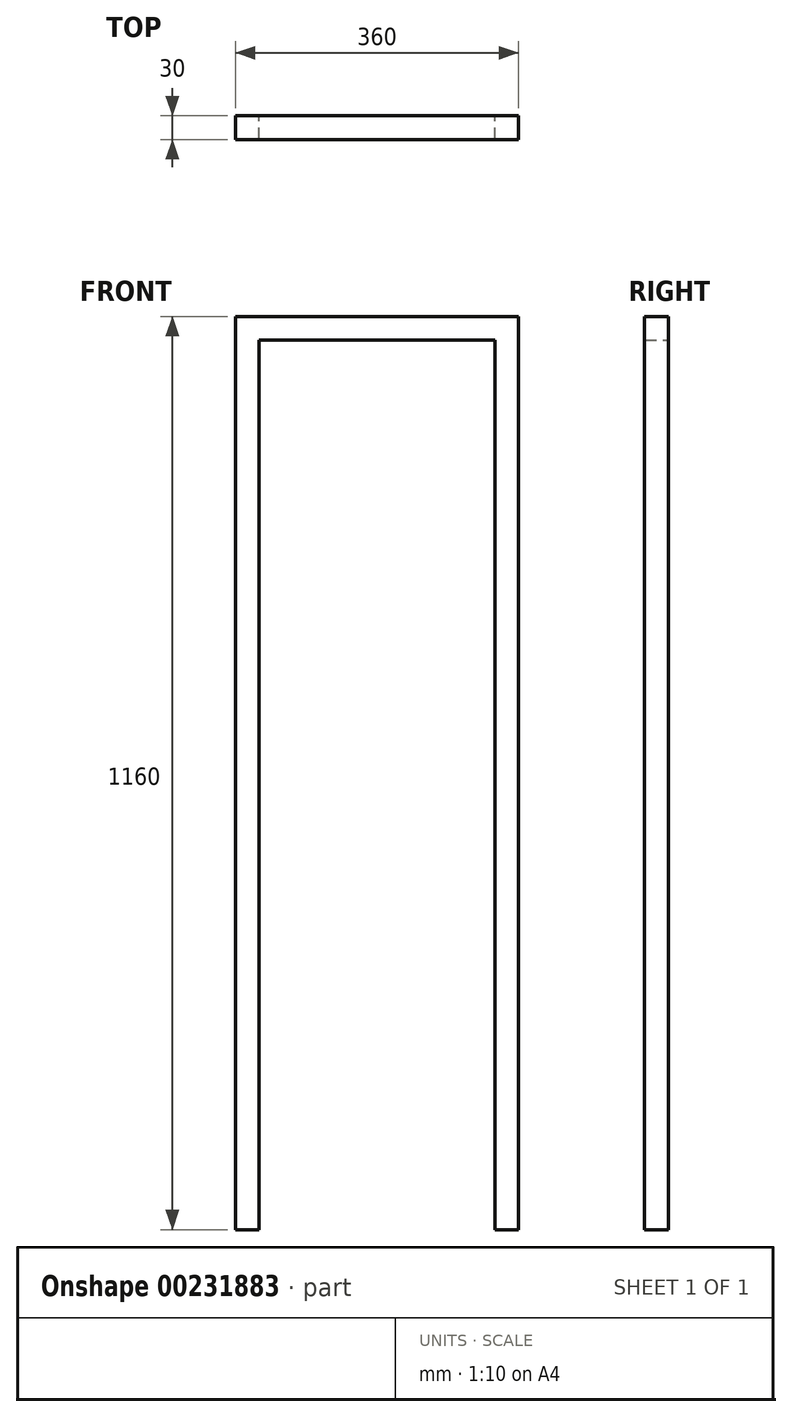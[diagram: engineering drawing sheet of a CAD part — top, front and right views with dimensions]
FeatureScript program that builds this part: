
annotation { "Feature Type Name" : "Feature", "Feature Type Description" : "" }
export const myFeature = defineFeature(function(context is Context, id is Id, definition is map)
    precondition{}
    {
        {
            var Q0;
            Q0=qCreatedBy(makeId("Front.planeOp"),FACE);
            var sketch = newSketch(context, id + "F0", { "sketchPlane" : qUnion([Q0])});
            skLineSegment(sketch, "E0.top", {"start": v(0, 1130) * mm, "end": v(-300, 1130) * mm});
            skLineSegment(sketch, "E0.left", {"start": v(0, 0) * mm, "end": v(0, 1130) * mm});
            skLineSegment(sketch, "E0.right", {"start": v(-300, 0) * mm, "end": v(-300, 1130) * mm});
            skLineSegment(sketch, "E1.0", {"start": v(-330, 0) * mm, "end": v(-330, 1160) * mm});
            skLineSegment(sketch, "E1.1", {"start": v(30, 1160) * mm, "end": v(-330, 1160) * mm});
            skLineSegment(sketch, "E1.2", {"start": v(30, 0) * mm, "end": v(30, 1160) * mm});
            skLineSegment(sketch, "E2", {"start": v(-300, 0) * mm, "end": v(-330, 0) * mm});
            skLineSegment(sketch, "E3", {"start": v(0, 0) * mm, "end": v(30, 0) * mm});
            skSolve(sketch);
        }
        {
            var Q0;
            Q0 = qSketchRegion(id + "F0", true);
            extrude(context, id + "F1", {"entities" : qUnion([Q0]), "depth" : 30 * mm});
        }
    });
